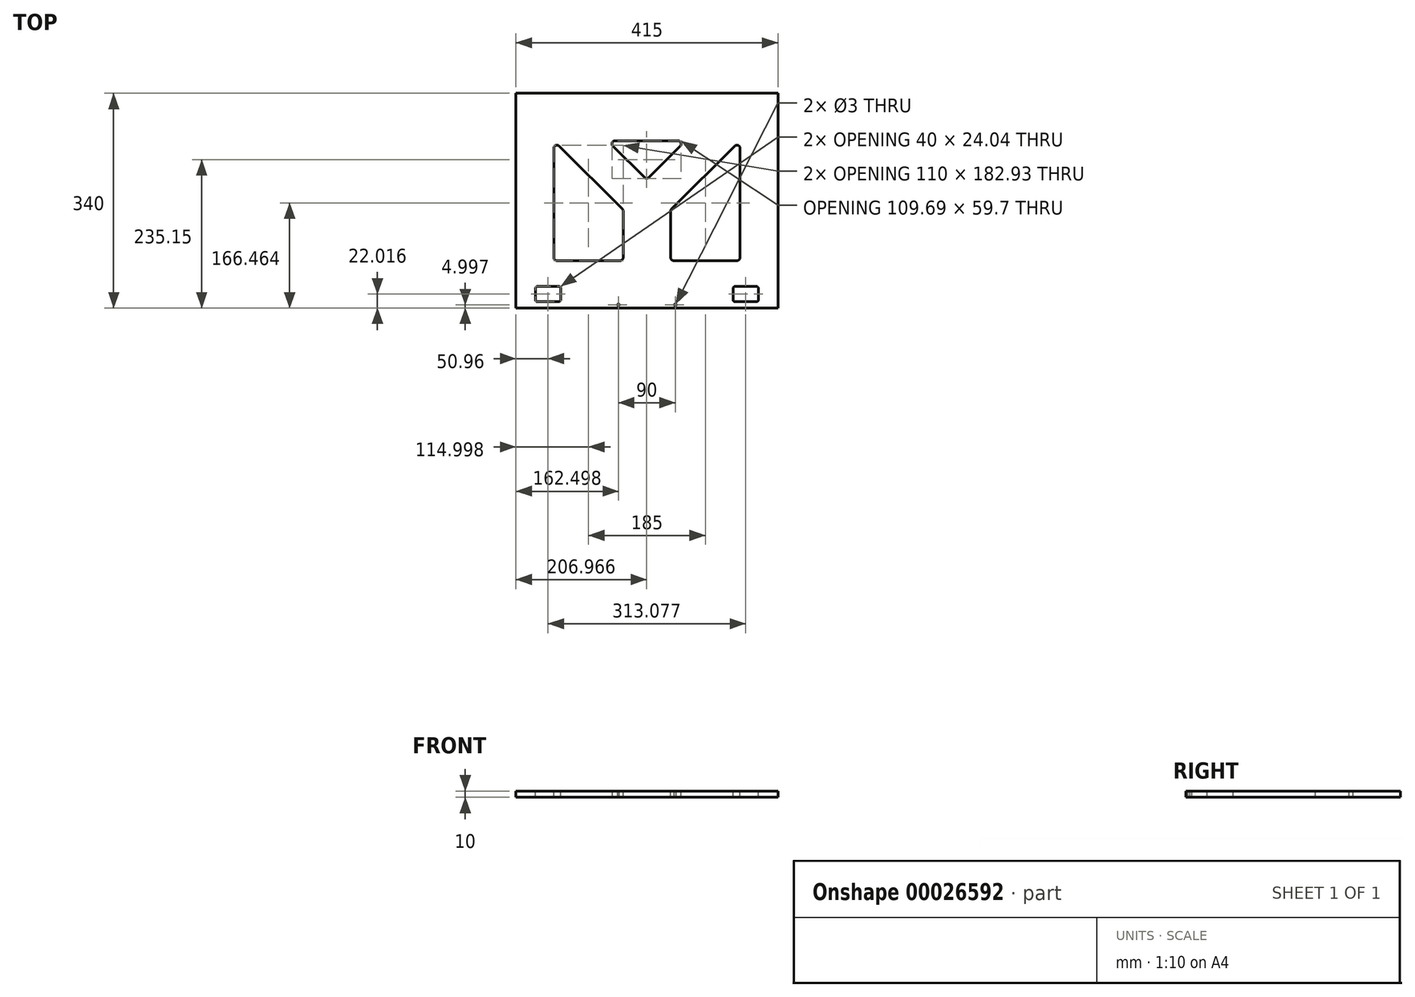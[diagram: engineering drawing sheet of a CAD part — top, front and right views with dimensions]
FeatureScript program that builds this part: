
annotation { "Feature Type Name" : "Feature", "Feature Type Description" : "" }
export const myFeature = defineFeature(function(context is Context, id is Id, definition is map)
    precondition{}
    {
        {
            var Q0;
            Q0=qCreatedBy(makeId("Top.planeOp"),FACE);
            var sketch = newSketch(context, id + "F0", { "sketchPlane" : qUnion([Q0])});
            skLineSegment(sketch, "E0.bottom", {"start": v(-70.96, 65.05) * mm, "end": v(344.04, 65.05) * mm});
            skLineSegment(sketch, "E0.top", {"start": v(-70.96, -274.95) * mm, "end": v(344.04, -274.95) * mm});
            skLineSegment(sketch, "E0.left", {"start": v(-70.96, 65.05) * mm, "end": v(-70.96, -274.95) * mm});
            skLineSegment(sketch, "E0.right", {"start": v(344.04, 65.05) * mm, "end": v(344.04, -274.95) * mm});
            skSolve(sketch);
        }
        {
            var Q0;
            Q0=qSketchRegion(id+"F0",true);
            extrude(context, id + "F1", {"entities" : qUnion([Q0]), "depth" : 10 * mm});
        }
        {
            var Q0;
            Q0=makeQuery(id+"F1.opExtrude","CAP_FACE",FACE,{"disambiguationData":[OSD([sQuery(id+"F0.wireOp",EDGE,"E0.bottom"),sQuery(id+"F0.wireOp",EDGE,"E0.top"),sQuery(id+"F0.wireOp",EDGE,"E0.left"),sQuery(id+"F0.wireOp",EDGE,"E0.right")])],"isStart":false});
            var sketch = newSketch(context, id + "F2", { "sketchPlane" : qUnion([Q0])});
            skLineSegment(sketch, "E1.bottom", {"start": v(-70.96, 65.05) * mm, "end": v(344.04, 65.05) * mm, "construction": true});
            skLineSegment(sketch, "E1.top", {"start": v(-70.96, -274.95) * mm, "end": v(344.04, -274.95) * mm, "construction": true});
            skLineSegment(sketch, "E1.left", {"start": v(-70.96, 65.05) * mm, "end": v(-70.96, -274.95) * mm, "construction": true});
            skLineSegment(sketch, "E1.right", {"start": v(344.04, 65.05) * mm, "end": v(344.04, -274.95) * mm, "construction": true});
            skLineSegment(sketch, "E2", {"start": v(-10.96, -9.95) * mm, "end": v(99.04, -119.57) * mm});
            skLineSegment(sketch, "E3", {"start": v(284.04, -9.95) * mm, "end": v(174.04, -119.57) * mm});
            skLineSegment(sketch, "E4.0", {"start": v(174.04, -199.95) * mm, "end": v(174.04, -119.57) * mm});
            skLineSegment(sketch, "E5.0", {"start": v(99.04, -199.95) * mm, "end": v(99.04, -119.57) * mm});
            skPoint(sketch, "E6.orphan", {"position": v(136.54, -9.95) * mm});
            skLineSegment(sketch, "E7.0", {"start": v(74.04, -9.95) * mm, "end": v(136, -71.7) * mm});
            skLineSegment(sketch, "E8.0", {"start": v(197.97, -9.95) * mm, "end": v(136, -71.7) * mm});
            skPoint(sketch, "E9.start.orphan", {"position": v(136, -215.36) * mm});
            skLineSegment(sketch, "E10", {"start": v(-10.96, -9.95) * mm, "end": v(-10.96, -199.95) * mm});
            skLineSegment(sketch, "E11", {"start": v(-10.96, -199.95) * mm, "end": v(99.04, -199.95) * mm});
            skLineSegment(sketch, "E12", {"start": v(174.04, -199.95) * mm, "end": v(284.04, -199.95) * mm});
            skLineSegment(sketch, "E13", {"start": v(284.04, -199.95) * mm, "end": v(284.04, -9.95) * mm});
            skLineSegment(sketch, "E14", {"start": v(197.97, -9.95) * mm, "end": v(74.04, -9.95) * mm});
            skSolve(sketch);
        }
        {
            var Q0;
            Q0=makeQuery(id+"F1.opExtrude","CAP_FACE",FACE,{"disambiguationData":[OSD([sQuery(id+"F0.wireOp",EDGE,"E0.bottom"),sQuery(id+"F0.wireOp",EDGE,"E0.top"),sQuery(id+"F0.wireOp",EDGE,"E0.left"),sQuery(id+"F0.wireOp",EDGE,"E0.right")])],"isStart":false});
            var sketch = newSketch(context, id + "F3", { "sketchPlane" : qUnion([Q0])});
            skLineSegment(sketch, "E15.bottom", {"start": v(-37, -240.92) * mm, "end": v(-3, -240.92) * mm});
            skLineSegment(sketch, "E15.top", {"start": v(-37, -264.95) * mm, "end": v(-3, -264.95) * mm});
            skLineSegment(sketch, "E15.left", {"start": v(-40, -243.92) * mm, "end": v(-40, -261.95) * mm});
            skLineSegment(sketch, "E15.right", {"start": v(0, -243.92) * mm, "end": v(0, -261.95) * mm});
            skPoint(sketch, "E16.visualSharp", {"position": v(-40, -240.92) * mm});
            skArc(sketch, "E16.filletArc", {"start": v(-37, -240.92) * mm, "mid": v(-39.12, -241.8) * mm, "end": v(-40, -243.92) * mm});
            skPoint(sketch, "E17.visualSharp", {"position": v(0, -240.92) * mm});
            skArc(sketch, "E17.filletArc", {"start": v(0, -243.92) * mm, "mid": v(-0.88, -241.8) * mm, "end": v(-3, -240.92) * mm});
            skPoint(sketch, "E18.visualSharp", {"position": v(0, -264.95) * mm});
            skArc(sketch, "E18.filletArc", {"start": v(-3, -264.95) * mm, "mid": v(-0.88, -264.07) * mm, "end": v(0, -261.95) * mm});
            skPoint(sketch, "E19.visualSharp", {"position": v(-40, -264.95) * mm});
            skArc(sketch, "E19.filletArc", {"start": v(-40, -261.95) * mm, "mid": v(-39.12, -264.07) * mm, "end": v(-37, -264.95) * mm});
            skLineSegment(sketch, "E20", {"start": v(136.54, 65.05) * mm, "end": v(136.54, -274.95) * mm, "construction": true});
            skArc(sketch, "E21.MirrorCS", {"start": v(313.08, -261.95) * mm, "mid": v(312.2, -264.07) * mm, "end": v(310.08, -264.95) * mm});
            skArc(sketch, "E22.MirrorCS", {"start": v(276.08, -264.95) * mm, "mid": v(273.96, -264.07) * mm, "end": v(273.08, -261.95) * mm});
            skArc(sketch, "E23.MirrorCS", {"start": v(273.08, -243.92) * mm, "mid": v(273.96, -241.8) * mm, "end": v(276.08, -240.92) * mm});
            skArc(sketch, "E24.MirrorCS", {"start": v(310.08, -240.92) * mm, "mid": v(312.2, -241.8) * mm, "end": v(313.08, -243.92) * mm});
            skLineSegment(sketch, "E25.MirrorCS", {"start": v(273.08, -243.92) * mm, "end": v(273.08, -261.95) * mm});
            skLineSegment(sketch, "E26.MirrorCS", {"start": v(313.08, -243.92) * mm, "end": v(313.08, -261.95) * mm});
            skPoint(sketch, "E27.MirrorP", {"position": v(273.08, -264.95) * mm});
            skPoint(sketch, "E28.MirrorP", {"position": v(273.08, -240.92) * mm});
            skPoint(sketch, "E29.MirrorP", {"position": v(313.08, -240.92) * mm});
            skPoint(sketch, "E30.MirrorP", {"position": v(313.08, -264.95) * mm});
            skLineSegment(sketch, "E31.MirrorCS", {"start": v(310.08, -240.92) * mm, "end": v(276.08, -240.92) * mm});
            skLineSegment(sketch, "E32.MirrorCS", {"start": v(310.08, -264.95) * mm, "end": v(276.08, -264.95) * mm});
            skSolve(sketch);
        }
        {
            var Q0;
            Q0=qSketchRegion(id+"F2",true);
            extrude(context, id + "F4", {"entities" : qUnion([Q0]), "operationType" : NewBodyOperationType.REMOVE, "endBound" : BoundingType.THROUGH_ALL, "oppositeDirection" : true, "depth" : 25 * mm});
        }
        {
            var Q0;
            Q0=qSketchRegion(id+"F3",true);
            extrude(context, id + "F5", {"entities" : qUnion([Q0]), "operationType" : NewBodyOperationType.REMOVE, "endBound" : BoundingType.THROUGH_ALL, "oppositeDirection" : true, "depth" : 25 * mm});
        }
        {
            var Q0;
            Q0=makeQuery(id+"F4.boolean.opBoolean","COPY",EDGE,{"derivedFrom":makeQuery(id+"F4.opExtrude","SWEPT_EDGE",EDGE,{"disambiguationData":[OSD([sQuery(id+"F2.wireOp",EDGE,"E2"),sQuery(id+"F2.wireOp",EDGE,"E10")])]})});
            var Q1;
            Q1=makeQuery(id+"F4.boolean.opBoolean","COPY",EDGE,{"derivedFrom":makeQuery(id+"F4.opExtrude","SWEPT_EDGE",EDGE,{"disambiguationData":[OSD([sQuery(id+"F2.wireOp",EDGE,"E10"),sQuery(id+"F2.wireOp",EDGE,"E11")])]})});
            var Q2;
            Q2=makeQuery(id+"F4.boolean.opBoolean","COPY",EDGE,{"derivedFrom":makeQuery(id+"F4.opExtrude","SWEPT_EDGE",EDGE,{"disambiguationData":[OSD([sQuery(id+"F2.wireOp",EDGE,"E5.0"),sQuery(id+"F2.wireOp",EDGE,"E11")])]})});
            var Q3;
            Q3=makeQuery(id+"F4.boolean.opBoolean","COPY",EDGE,{"derivedFrom":makeQuery(id+"F4.opExtrude","SWEPT_EDGE",EDGE,{"disambiguationData":[OSD([sQuery(id+"F2.wireOp",EDGE,"E2"),sQuery(id+"F2.wireOp",EDGE,"E5.0")])]})});
            var Q4;
            Q4=makeQuery(id+"F4.boolean.opBoolean","COPY",EDGE,{"derivedFrom":makeQuery(id+"F4.opExtrude","SWEPT_EDGE",EDGE,{"disambiguationData":[OSD([sQuery(id+"F2.wireOp",EDGE,"E7.0"),sQuery(id+"F2.wireOp",EDGE,"E14")])]})});
            var Q5;
            Q5=makeQuery(id+"F4.boolean.opBoolean","COPY",EDGE,{"derivedFrom":makeQuery(id+"F4.opExtrude","SWEPT_EDGE",EDGE,{"disambiguationData":[OSD([sQuery(id+"F2.wireOp",EDGE,"E7.0"),sQuery(id+"F2.wireOp",EDGE,"E8.0")])]})});
            var Q6;
            Q6=makeQuery(id+"F4.boolean.opBoolean","COPY",EDGE,{"derivedFrom":makeQuery(id+"F4.opExtrude","SWEPT_EDGE",EDGE,{"disambiguationData":[OSD([sQuery(id+"F2.wireOp",EDGE,"E8.0"),sQuery(id+"F2.wireOp",EDGE,"E14")])]})});
            var Q7;
            Q7=makeQuery(id+"F4.boolean.opBoolean","COPY",EDGE,{"derivedFrom":makeQuery(id+"F4.opExtrude","SWEPT_EDGE",EDGE,{"disambiguationData":[OSD([sQuery(id+"F2.wireOp",EDGE,"E3"),sQuery(id+"F2.wireOp",EDGE,"E4.0")])]})});
            var Q8;
            Q8=makeQuery(id+"F4.boolean.opBoolean","COPY",EDGE,{"derivedFrom":makeQuery(id+"F4.opExtrude","SWEPT_EDGE",EDGE,{"disambiguationData":[OSD([sQuery(id+"F2.wireOp",EDGE,"E4.0"),sQuery(id+"F2.wireOp",EDGE,"E12")])]})});
            var Q9;
            Q9=makeQuery(id+"F4.boolean.opBoolean","COPY",EDGE,{"derivedFrom":makeQuery(id+"F4.opExtrude","SWEPT_EDGE",EDGE,{"disambiguationData":[OSD([sQuery(id+"F2.wireOp",EDGE,"E12"),sQuery(id+"F2.wireOp",EDGE,"E13")])]})});
            var Q10;
            Q10=makeQuery(id+"F4.boolean.opBoolean","COPY",EDGE,{"derivedFrom":makeQuery(id+"F4.opExtrude","SWEPT_EDGE",EDGE,{"disambiguationData":[OSD([sQuery(id+"F2.wireOp",EDGE,"E3"),sQuery(id+"F2.wireOp",EDGE,"E13")])]})});
            fillet(context, id + "F6", {"entities" : qUnion([Q0, Q1, Q2, Q3, Q4, Q5, Q6, Q7, Q8, Q9, Q10]), "radius" : 5 * mm, "tangentPropagation" : true, "allowEdgeOverflow" : false});
        }
        {
            var Q0;
            Q0=makeQuery(id+"F1.opExtrude","CAP_FACE",FACE,{"disambiguationData":[OSD([sQuery(id+"F0.wireOp",EDGE,"E0.bottom"),sQuery(id+"F0.wireOp",EDGE,"E0.top"),sQuery(id+"F0.wireOp",EDGE,"E0.left"),sQuery(id+"F0.wireOp",EDGE,"E0.right")])],"isStart":false});
            var sketch = newSketch(context, id + "F7", { "sketchPlane" : qUnion([Q0])});
            skLineSegment(sketch, "E33", {"start": v(136.54, 65.05) * mm, "end": v(136.54, -274.95) * mm, "construction": true});
            skCircle(sketch, "E34", {"center": v(91.54, -269.95) * mm, "radius": 1.5 * mm});
            skCircle(sketch, "E35.MirrorC", {"center": v(181.54, -269.95) * mm, "radius": 1.5 * mm});
            skSolve(sketch);
        }
        {
            var Q0;
            Q0=qSketchRegion(id+"F7",true);
            extrude(context, id + "F8", {"entities" : qUnion([Q0]), "operationType" : NewBodyOperationType.REMOVE, "endBound" : BoundingType.THROUGH_ALL, "oppositeDirection" : true, "depth" : 25 * mm});
        }
    });
